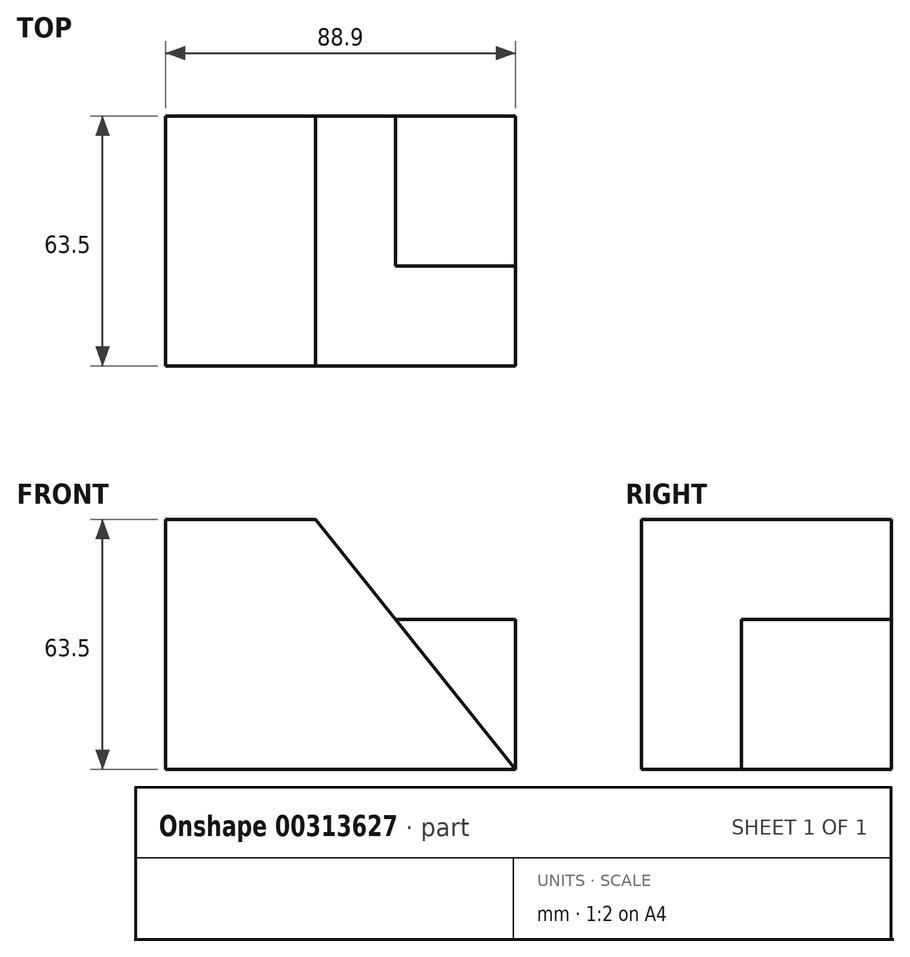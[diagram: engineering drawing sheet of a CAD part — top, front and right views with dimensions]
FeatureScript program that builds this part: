
annotation { "Feature Type Name" : "Feature", "Feature Type Description" : "" }
export const myFeature = defineFeature(function(context is Context, id is Id, definition is map)
    precondition{}
    {
        {
            var Q0;
            Q0=qCreatedBy(makeId("Front.planeOp"),FACE);
            var sketch = newSketch(context, id + "F0", { "sketchPlane" : qUnion([Q0])});
            skLineSegment(sketch, "E0", {"start": v(-54.94, -27.72) * mm, "end": v(33.96, -27.72) * mm});
            skLineSegment(sketch, "E1", {"start": v(-54.94, -27.72) * mm, "end": v(-54.94, 35.78) * mm});
            skLineSegment(sketch, "E2", {"start": v(-54.94, 35.78) * mm, "end": v(-16.84, 35.78) * mm});
            skLineSegment(sketch, "E3", {"start": v(-16.84, 35.78) * mm, "end": v(33.96, -27.72) * mm});
            skSolve(sketch);
        }
        {
            var Q0;
            Q0=makeQuery(id+"F0.imprint","IMPRINT",FACE,{"disambiguationData":[TD([[makeQuery(id+"F0.imprint","IMPRINT",EDGE,{"derivedFrom":sQuery(id+"F0.wireOp",EDGE,"E0")}),1.0]])]});
            extrude(context, id + "F1", {"entities" : qUnion([Q0]), "depth" : 63.5 * mm});
        }
        {
            var Q0;
            Q0=makeQuery(id+"F1.opExtrude","CAP_FACE",FACE,{"disambiguationData":[OSD([sQuery(id+"F0.wireOp",EDGE,"E0"),sQuery(id+"F0.wireOp",EDGE,"E1"),sQuery(id+"F0.wireOp",EDGE,"E2"),sQuery(id+"F0.wireOp",EDGE,"E3")])],"isStart":true});
            var sketch = newSketch(context, id + "F2", { "sketchPlane" : qUnion([Q0])});
            skLineSegment(sketch, "E4", {"start": v(-33.96, -27.72) * mm, "end": v(-33.96, 10.38) * mm});
            skLineSegment(sketch, "E5", {"start": v(-33.96, 10.38) * mm, "end": v(-3.48, 10.38) * mm});
            skSolve(sketch);
        }
        {
            var Q0;
            Q0 = qSketchRegion(id + "F2", true);
            var Q1;
            {var subQ0=sQuery(id+"F2.wireOp",EDGE,"E4");Q1=makeQuery(id+"F2.imprint","IMPRINT",FACE,{"disambiguationData":[TD([[makeQuery(id+"F2.imprint","IMPRINT",EDGE,{"derivedFrom":subQ0}),-1.0]])]});}
            extrude(context, id + "F3", {"entities" : qUnion([Q0, Q1]), "operationType" : NewBodyOperationType.ADD, "oppositeDirection" : true, "depth" : 38.1 * mm});
        }
    });
